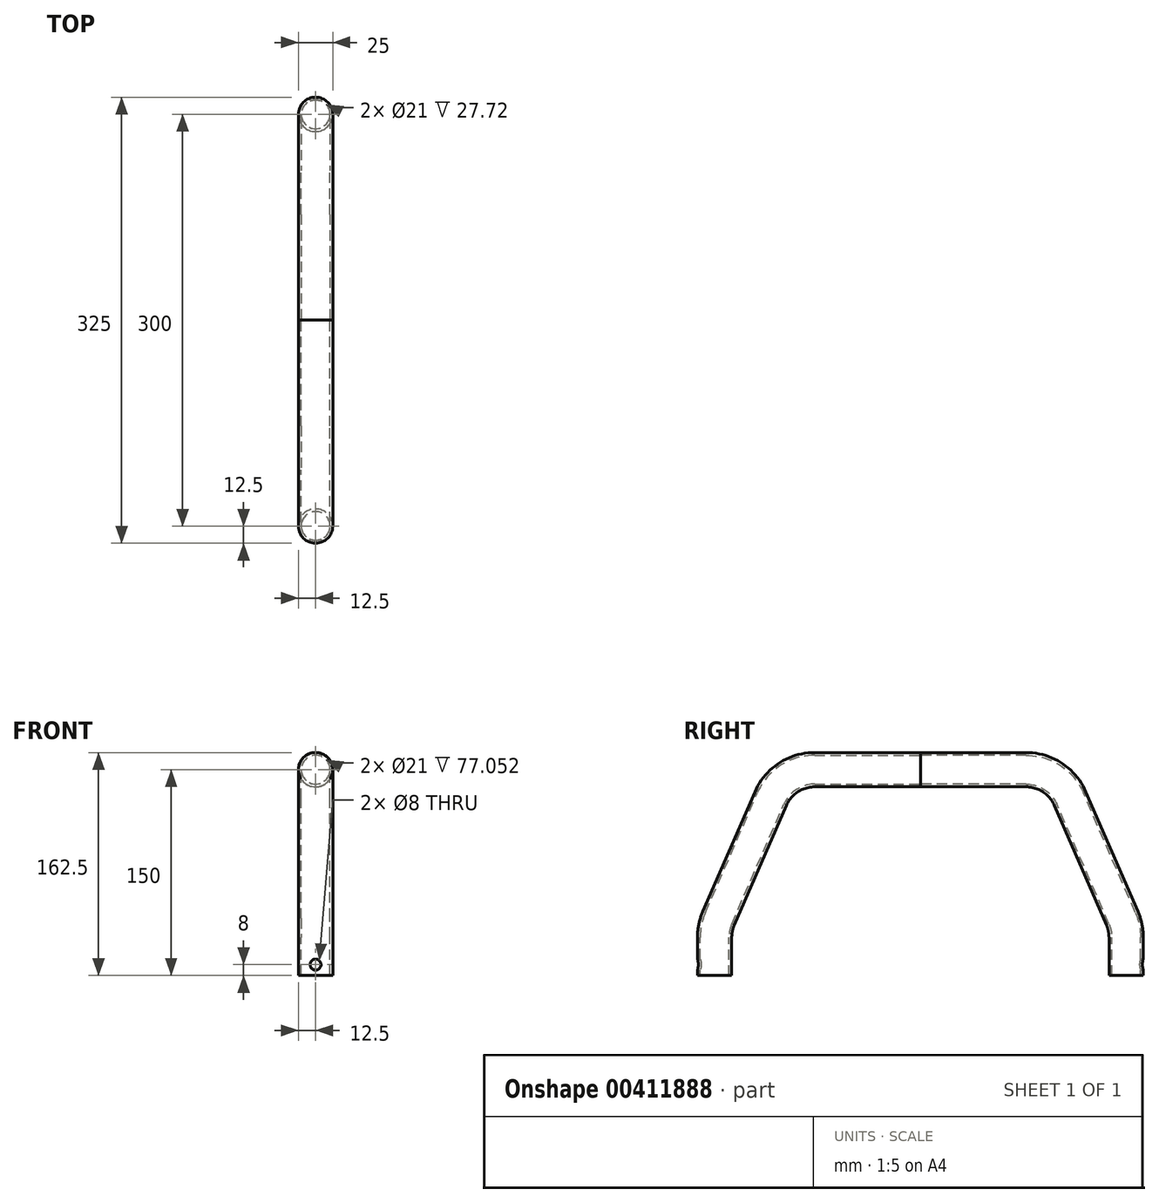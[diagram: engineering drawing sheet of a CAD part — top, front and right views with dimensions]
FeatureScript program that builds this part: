
annotation { "Feature Type Name" : "Feature", "Feature Type Description" : "" }
export const myFeature = defineFeature(function(context is Context, id is Id, definition is map)
    precondition{}
    {
        {
            var Q0;
            Q0=qCreatedBy(makeId("Right.planeOp"),FACE);
            var sketch = newSketch(context, id + "F0", { "sketchPlane" : qUnion([Q0])});
            skLineSegment(sketch, "E0", {"start": v(0, 0) * mm, "end": v(0, 187.78) * mm, "construction": true});
            skLineSegment(sketch, "E1", {"start": v(0, 150) * mm, "end": v(-77.05, 150) * mm});
            skLineSegment(sketch, "E2", {"start": v(-109.15, 128.96) * mm, "end": v(-147.1, 41.68) * mm});
            skLineSegment(sketch, "E3", {"start": v(-150, 27.72) * mm, "end": v(-150, 0) * mm});
            skPoint(sketch, "E4.visualSharp", {"position": v(-100, 150) * mm});
            skArc(sketch, "E4.filletArc", {"start": v(-77.05, 150) * mm, "mid": v(-96.24, 144.27) * mm, "end": v(-109.15, 128.96) * mm});
            skPoint(sketch, "E5.visualSharp", {"position": v(-150, 35) * mm});
            skArc(sketch, "E5.filletArc", {"start": v(-147.1, 41.68) * mm, "mid": v(-149.27, 34.85) * mm, "end": v(-150, 27.72) * mm});
            skSolve(sketch);
        }
        {
            var Q0;
            Q0=qCreatedBy(makeId("Top.planeOp"),FACE);
            var sketch = newSketch(context, id + "F1", { "sketchPlane" : qUnion([Q0])});
            skCircle(sketch, "E6", {"center": v(0, -150) * mm, "radius": 12.5 * mm});
            skCircle(sketch, "E7.0", {"center": v(0, -150) * mm, "radius": 10.5 * mm});
            skSolve(sketch);
        }
        {
            var Q0;
            Q0 = qSketchRegion(id + "F1", true);
            var Q1;
            Q1 = qConstructionFilter(qBodyType(qCreatedBy(id + "F0" ,EDGE), BodyType.WIRE), ConstructionObject.NO);
            sweep(context, id + "F2", {"profiles" : qUnion([Q0]), "path" : qUnion([Q1])});
        }
        {
            var Q0;
            Q0=qCreatedBy(makeId("Front.planeOp"),FACE);
            var Q1;
            Q1=sQuery(id+"F0.wireOp",VERTEX,"E3.end");
            cPlane(context, id + "F3", {"entities" : qUnion([Q0, Q1]), "cplaneType" : CPlaneType.PLANE_POINT, "offset" : 25 * mm, "width" : 150 * mm, "height" : 150 * mm});
        }
        {
            var Q0;
            Q0=qCreatedBy(id+"F3.planeOp",FACE);
            var sketch = newSketch(context, id + "F4", { "sketchPlane" : qUnion([Q0])});
            skCircle(sketch, "E8", {"center": v(0, 8) * mm, "radius": 4 * mm});
            skSolve(sketch);
        }
        {
            var Q0;
            Q0 = qSketchRegion(id + "F4", true);
            extrude(context, id + "F5", {"entities" : qUnion([Q0]), "operationType" : NewBodyOperationType.REMOVE, "endBound" : BoundingType.THROUGH_ALL, "depth" : 25 * mm});
        }
        {
            var Q0;
            Q0=makeQuery(id+"F2.opSweep","SWEPT_BODY",BODY,{"disambiguationData":[OSD([sQuery(id+"F0.wireOp",EDGE,"E3"),sQuery(id+"F1.wireOp",EDGE,"E6"),sQuery(id+"F1.wireOp",EDGE,"E7.0")])]});
            var Q1;
            Q1=qCreatedBy(makeId("Front.planeOp"),FACE);
            mirror(context, id + "F6", {"entities" : qUnion([Q0]), "mirrorPlane" : qUnion([Q1])});
        }
    });
